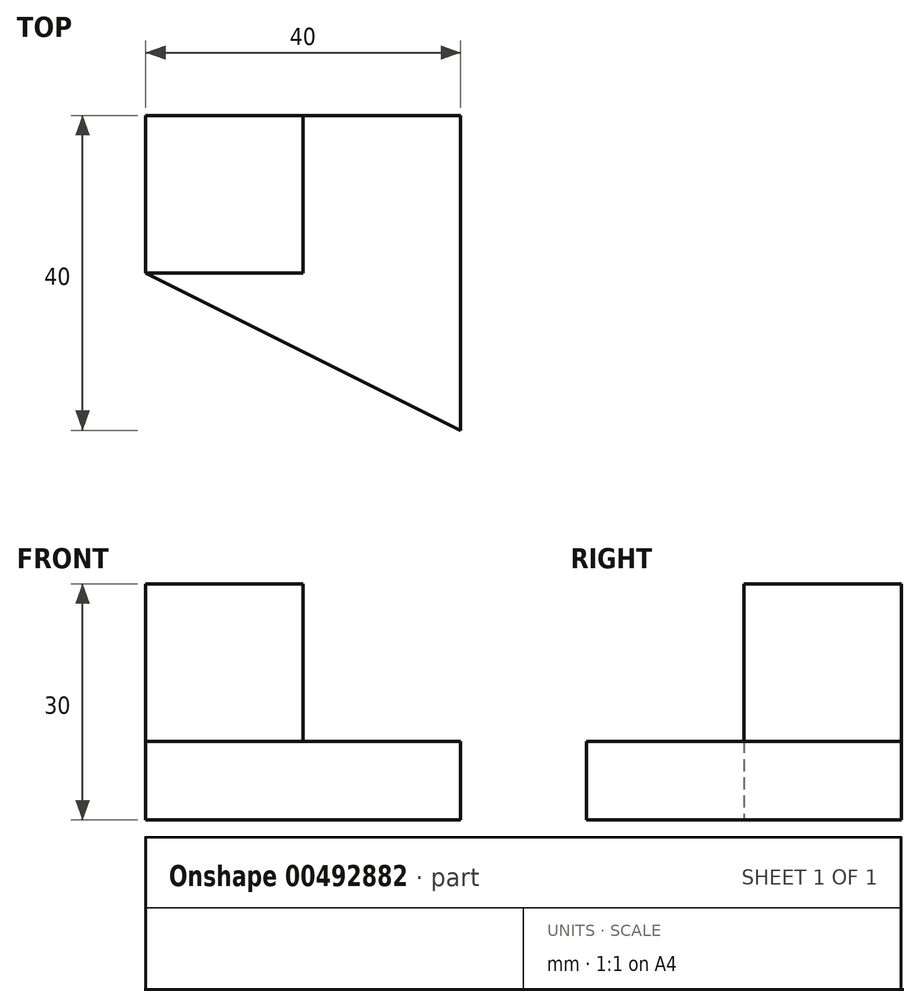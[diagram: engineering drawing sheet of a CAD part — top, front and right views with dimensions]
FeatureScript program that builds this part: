
annotation { "Feature Type Name" : "Feature", "Feature Type Description" : "" }
export const myFeature = defineFeature(function(context is Context, id is Id, definition is map)
    precondition{}
    {
        {
            var Q0;
            Q0=qCreatedBy(makeId("Top.planeOp"),FACE);
            var sketch = newSketch(context, id + "F0", { "sketchPlane" : qUnion([Q0])});
            skLineSegment(sketch, "E0", {"start": v(0, 0) * mm, "end": v(0, 20) * mm});
            skLineSegment(sketch, "E1", {"start": v(0, 20) * mm, "end": v(40, 20) * mm});
            skLineSegment(sketch, "E2", {"start": v(40, 20) * mm, "end": v(40, -20) * mm});
            skLineSegment(sketch, "E3", {"start": v(40, -20) * mm, "end": v(0, 0) * mm});
            skSolve(sketch);
        }
        {
            var Q0;
            Q0=makeQuery(id+"F0.imprint","IMPRINT",FACE,{"disambiguationData":[TD([[makeQuery(id+"F0.imprint","IMPRINT",EDGE,{"derivedFrom":sQuery(id+"F0.wireOp",EDGE,"E0")}),-1.0]])]});
            extrude(context, id + "F1", {"entities" : qUnion([Q0]), "depth" : 10 * mm});
        }
        {
            var Q0;
            Q0=makeQuery(id+"F1.opExtrude","CAP_FACE",FACE,{"disambiguationData":[OSD([sQuery(id+"F0.wireOp",EDGE,"E0"),sQuery(id+"F0.wireOp",EDGE,"E1"),sQuery(id+"F0.wireOp",EDGE,"E2"),sQuery(id+"F0.wireOp",EDGE,"E3")])],"isStart":false});
            var sketch = newSketch(context, id + "F2", { "sketchPlane" : qUnion([Q0])});
            skLineSegment(sketch, "E4", {"start": v(0, 20) * mm, "end": v(0, 0) * mm});
            skLineSegment(sketch, "E5", {"start": v(0, 0) * mm, "end": v(20, 0) * mm});
            skLineSegment(sketch, "E6", {"start": v(20, 0) * mm, "end": v(20, 20) * mm});
            skPoint(sketch, "E6.endSnap0", {"position": v(20, 20) * mm});
            skLineSegment(sketch, "E7", {"start": v(20, 20) * mm, "end": v(0, 20) * mm});
            skSolve(sketch);
        }
        {
            var Q0;
            Q0 = qSketchRegion(id + "F2", true);
            extrude(context, id + "F3", {"entities" : qUnion([Q0]), "operationType" : NewBodyOperationType.ADD, "depth" : 20 * mm});
        }
    });
